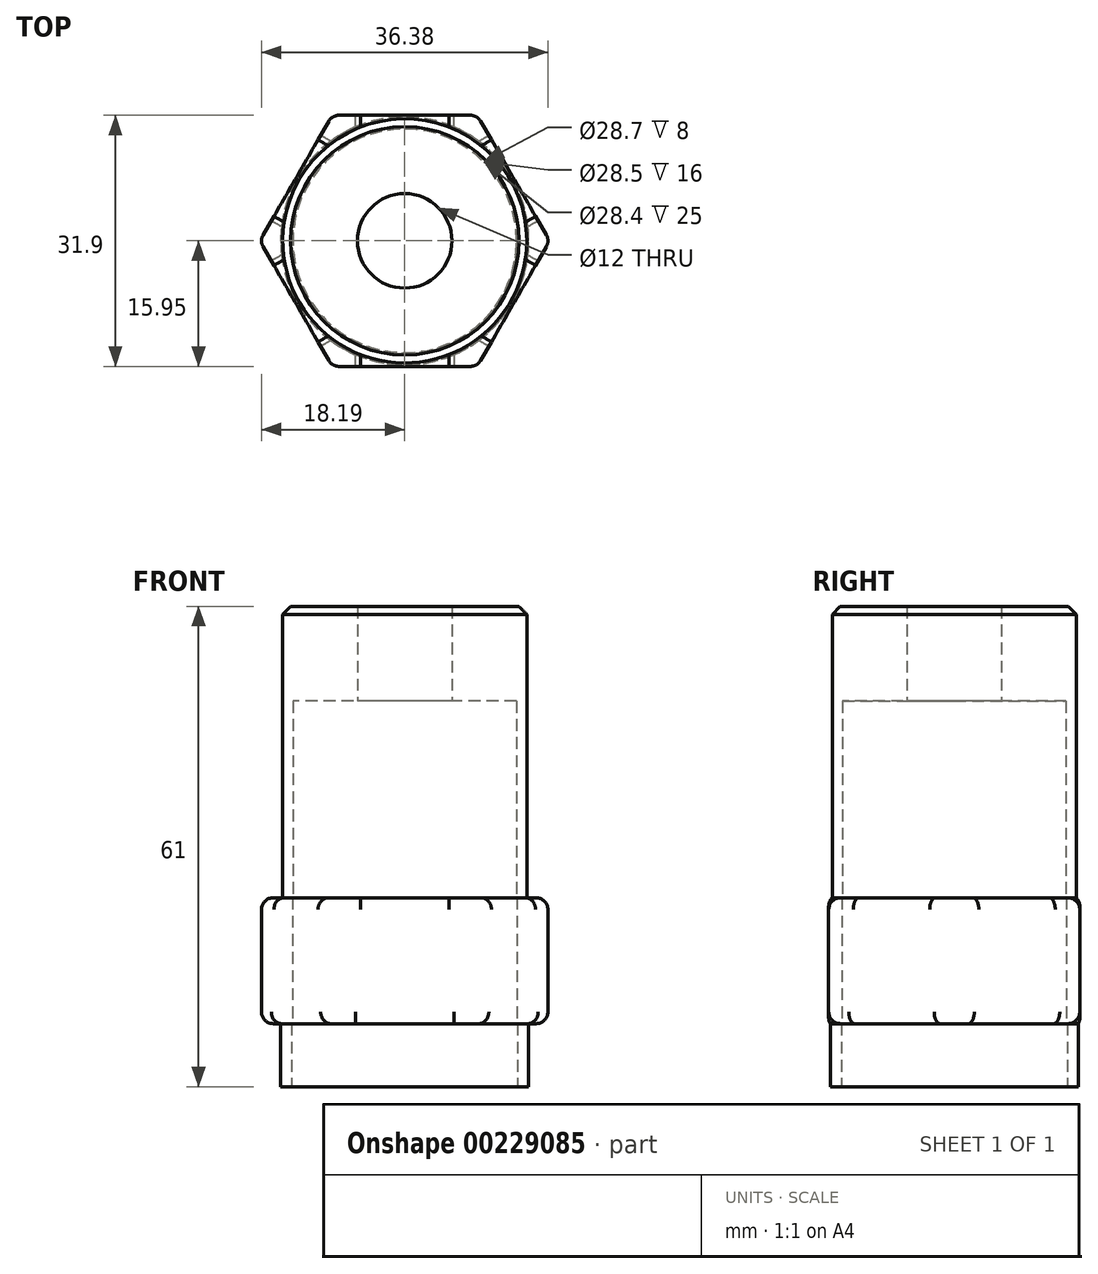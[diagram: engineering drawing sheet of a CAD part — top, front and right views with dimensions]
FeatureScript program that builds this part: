
annotation { "Feature Type Name" : "Feature", "Feature Type Description" : "" }
export const myFeature = defineFeature(function(context is Context, id is Id, definition is map)
    precondition{}
    {
        {
            var Q0;
            Q0=qCreatedBy(makeId("Top.planeOp"),FACE);
            var sketch = newSketch(context, id + "F0", { "sketchPlane" : qUnion([Q0])});
            skCircle(sketch, "E0", {"center": v(0, 0) * mm, "radius": 15.75 * mm});
            skCircle(sketch, "E1", {"center": v(0, 0) * mm, "radius": 14.35 * mm});
            skSolve(sketch);
        }
        {
            var Q0;
            Q0 = qSketchRegion(id + "F0", true);
            extrude(context, id + "F1", {"entities" : qUnion([Q0]), "depth" : 8 * mm});
        }
        {
            var Q0;
            Q0=makeQuery(id+"F1.opExtrude","CAP_FACE",FACE,{"disambiguationData":[OSD([sQuery(id+"F0.wireOp",EDGE,"E0"),sQuery(id+"F0.wireOp",EDGE,"E1")])],"isStart":false});
            var sketch = newSketch(context, id + "F2", { "sketchPlane" : qUnion([Q0])});
            skCircle(sketch, "E2.cCircle", {"center": v(0, 0) * mm, "radius": 15.95 * mm, "construction": true});
            skLineSegment(sketch, "E2.0", {"start": v(-9.2, 15.95) * mm, "end": v(9.2, 15.95) * mm});
            skLineSegment(sketch, "E2.1", {"start": v(9.2, 15.95) * mm, "end": v(18.42, 0) * mm});
            skLineSegment(sketch, "E2.2", {"start": v(18.42, 0) * mm, "end": v(9.2, -15.95) * mm});
            skLineSegment(sketch, "E2.3", {"start": v(9.2, -15.95) * mm, "end": v(-9.2, -15.95) * mm});
            skLineSegment(sketch, "E2.4", {"start": v(-9.2, -15.95) * mm, "end": v(-18.42, 0) * mm});
            skLineSegment(sketch, "E2.5", {"start": v(-18.42, 0) * mm, "end": v(-9.2, 15.95) * mm});
            skPoint(sketch, "E2.0.midPoint", {"position": v(0, 15.95) * mm});
            skCircle(sketch, "E3", {"center": v(0, 0) * mm, "radius": 14.25 * mm});
            skSolve(sketch);
        }
        {
            var Q0;
            Q0 = qSketchRegion(id + "F2", true);
            extrude(context, id + "F3", {"entities" : qUnion([Q0]), "operationType" : NewBodyOperationType.ADD, "depth" : 16 * mm});
        }
        {
            var Q0;
            Q0=makeQuery(id+"F3.opExtrude","CAP_FACE",FACE,{"disambiguationData":[OSD([sQuery(id+"F2.wireOp",EDGE,"E2.0"),sQuery(id+"F2.wireOp",EDGE,"E2.1"),sQuery(id+"F2.wireOp",EDGE,"E2.2"),sQuery(id+"F2.wireOp",EDGE,"E2.3"),sQuery(id+"F2.wireOp",EDGE,"E2.4"),sQuery(id+"F2.wireOp",EDGE,"E2.5"),sQuery(id+"F2.wireOp",EDGE,"E3")])],"isStart":false});
            var sketch = newSketch(context, id + "F4", { "sketchPlane" : qUnion([Q0])});
            skCircle(sketch, "E4", {"center": v(0, 0) * mm, "radius": 14.2 * mm});
            skCircle(sketch, "E5", {"center": v(0, 0) * mm, "radius": 15.5 * mm});
            skSolve(sketch);
        }
        {
            var Q0;
            Q0 = qSketchRegion(id + "F4", true);
            extrude(context, id + "F5", {"entities" : qUnion([Q0]), "operationType" : NewBodyOperationType.ADD, "depth" : 25 * mm});
        }
        {
            var Q0;
            Q0=makeQuery(id+"F5.opExtrude","CAP_FACE",FACE,{"disambiguationData":[OSD([sQuery(id+"F4.wireOp",EDGE,"E4"),sQuery(id+"F4.wireOp",EDGE,"E5")])],"isStart":false});
            var sketch = newSketch(context, id + "F6", { "sketchPlane" : qUnion([Q0])});
            skCircle(sketch, "E6", {"center": v(0, 0) * mm, "radius": 15.5 * mm});
            skCircle(sketch, "E7", {"center": v(0, 0) * mm, "radius": 6 * mm});
            skSolve(sketch);
        }
        {
            var Q0;
            Q0 = qSketchRegion(id + "F6", true);
            extrude(context, id + "F7", {"entities" : qUnion([Q0]), "operationType" : NewBodyOperationType.ADD, "depth" : 12 * mm});
        }
        {
            var Q0;
            Q0=makeQuery(id+"F3.opExtrude","SWEPT_EDGE",EDGE,{"disambiguationData":[OSD([sQuery(id+"F2.wireOp",EDGE,"E2.1"),sQuery(id+"F2.wireOp",EDGE,"E2.2")])]});
            var Q1;
            Q1=makeQuery(id+"F3.opExtrude","SWEPT_EDGE",EDGE,{"disambiguationData":[OSD([sQuery(id+"F2.wireOp",EDGE,"E2.2"),sQuery(id+"F2.wireOp",EDGE,"E2.3")])]});
            var Q2;
            Q2=makeQuery(id+"F3.opExtrude","SWEPT_EDGE",EDGE,{"disambiguationData":[OSD([sQuery(id+"F2.wireOp",EDGE,"E2.3"),sQuery(id+"F2.wireOp",EDGE,"E2.4")])]});
            var Q3;
            Q3=makeQuery(id+"F3.opExtrude","SWEPT_EDGE",EDGE,{"disambiguationData":[OSD([sQuery(id+"F2.wireOp",EDGE,"E2.0"),sQuery(id+"F2.wireOp",EDGE,"E2.1")])]});
            var Q4;
            Q4=makeQuery(id+"F3.opExtrude","SWEPT_EDGE",EDGE,{"disambiguationData":[OSD([sQuery(id+"F2.wireOp",EDGE,"E2.0"),sQuery(id+"F2.wireOp",EDGE,"E2.5")])]});
            var Q5;
            Q5=makeQuery(id+"F3.opExtrude","SWEPT_EDGE",EDGE,{"disambiguationData":[OSD([sQuery(id+"F2.wireOp",EDGE,"E2.4"),sQuery(id+"F2.wireOp",EDGE,"E2.5")])]});
            var Q6;
            Q6=makeQuery(id+"F3.opExtrude","CAP_EDGE",EDGE,{"disambiguationData":[OSD([sQuery(id+"F2.wireOp",EDGE,"E2.0")])],"isStart":false});
            var Q7;
            Q7=makeQuery(id+"F3.opExtrude","CAP_EDGE",EDGE,{"disambiguationData":[OSD([sQuery(id+"F2.wireOp",EDGE,"E2.1")])],"isStart":false});
            var Q8;
            Q8=makeQuery(id+"F3.opExtrude","CAP_EDGE",EDGE,{"disambiguationData":[OSD([sQuery(id+"F2.wireOp",EDGE,"E2.2")])],"isStart":false});
            var Q9;
            Q9=makeQuery(id+"F3.opExtrude","CAP_EDGE",EDGE,{"disambiguationData":[OSD([sQuery(id+"F2.wireOp",EDGE,"E2.3")])],"isStart":false});
            var Q10;
            Q10=makeQuery(id+"F3.opExtrude","CAP_EDGE",EDGE,{"disambiguationData":[OSD([sQuery(id+"F2.wireOp",EDGE,"E2.4")])],"isStart":false});
            var Q11;
            Q11=makeQuery(id+"F3.opExtrude","CAP_EDGE",EDGE,{"disambiguationData":[OSD([sQuery(id+"F2.wireOp",EDGE,"E2.5")])],"isStart":false});
            var Q12;
            Q12=makeQuery(id+"F3.opExtrude","CAP_EDGE",EDGE,{"disambiguationData":[OSD([sQuery(id+"F2.wireOp",EDGE,"E2.5")])],"isStart":true});
            var Q13;
            Q13=makeQuery(id+"F3.opExtrude","CAP_EDGE",EDGE,{"disambiguationData":[OSD([sQuery(id+"F2.wireOp",EDGE,"E2.0")])],"isStart":true});
            var Q14;
            Q14=makeQuery(id+"F3.opExtrude","CAP_EDGE",EDGE,{"disambiguationData":[OSD([sQuery(id+"F2.wireOp",EDGE,"E2.4")])],"isStart":true});
            var Q15;
            Q15=makeQuery(id+"F3.opExtrude","CAP_EDGE",EDGE,{"disambiguationData":[OSD([sQuery(id+"F2.wireOp",EDGE,"E2.3")])],"isStart":true});
            var Q16;
            Q16=makeQuery(id+"F3.opExtrude","CAP_EDGE",EDGE,{"disambiguationData":[OSD([sQuery(id+"F2.wireOp",EDGE,"E2.2")])],"isStart":true});
            var Q17;
            Q17=makeQuery(id+"F3.opExtrude","CAP_EDGE",EDGE,{"disambiguationData":[OSD([sQuery(id+"F2.wireOp",EDGE,"E2.1")])],"isStart":true});
            fillet(context, id + "F8", {"entities" : qUnion([Q0, Q1, Q2, Q3, Q4, Q5, Q6, Q7, Q8, Q9, Q10, Q11, Q12, Q13, Q14, Q15, Q16, Q17]), "radius" : 1.5 * mm, "tangentPropagation" : true, "allowEdgeOverflow" : false});
        }
        {
            var Q0;
            Q0=makeQuery(id+"F7.opExtrude","CAP_EDGE",EDGE,{"disambiguationData":[OSD([sQuery(id+"F6.wireOp",EDGE,"E6")])],"isStart":false});
            chamfer(context, id + "F9", {"entities" : qUnion([Q0]), "width" : 1 * mm, "tangentPropagation" : true});
        }
    });
